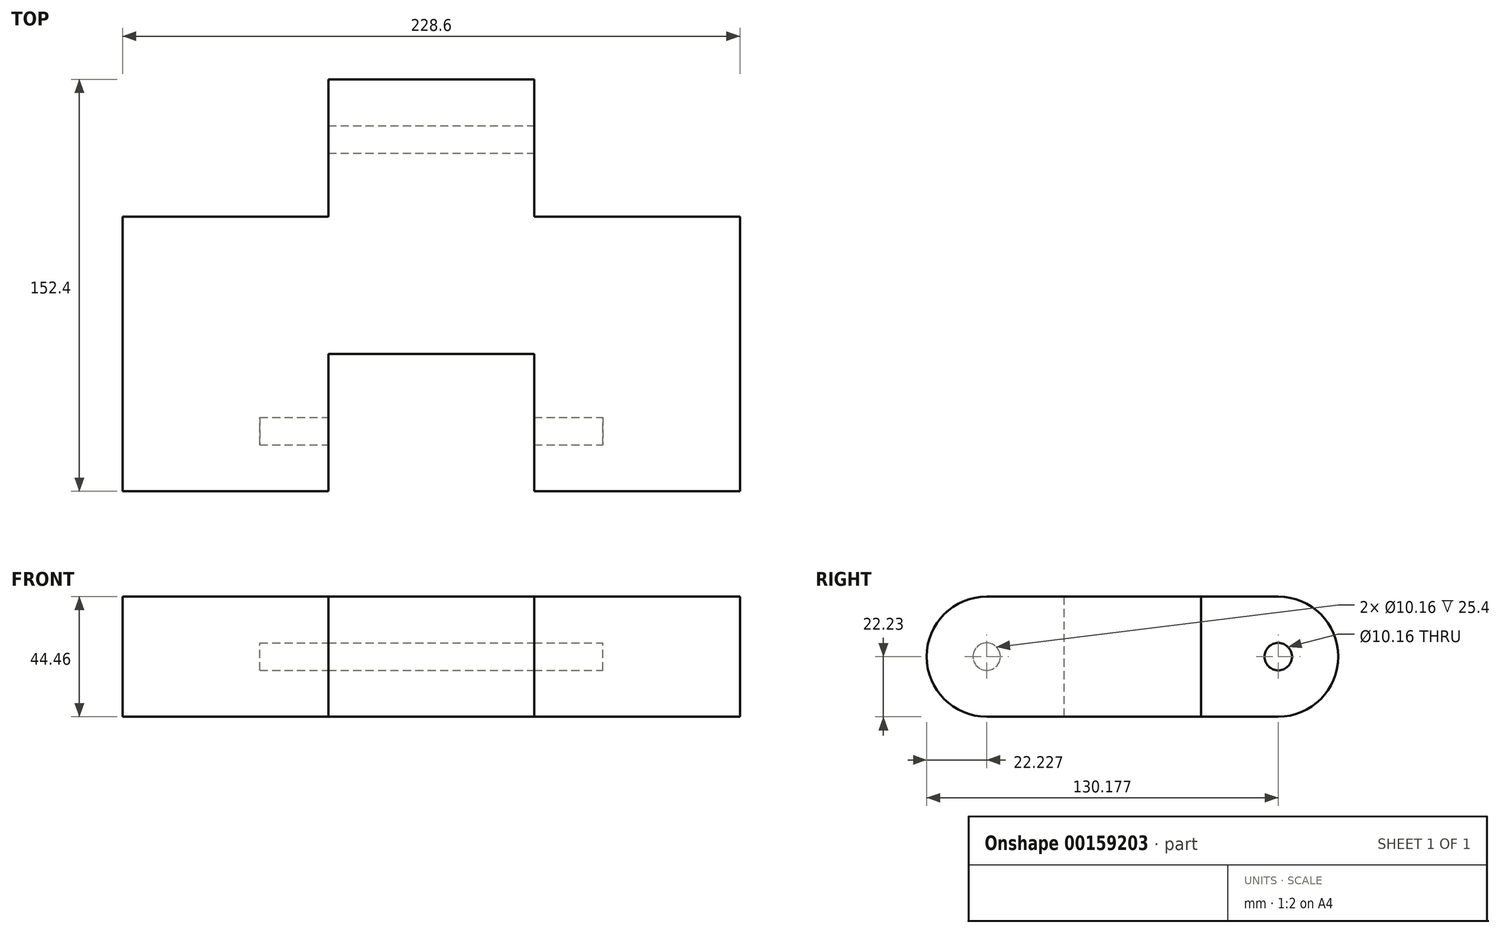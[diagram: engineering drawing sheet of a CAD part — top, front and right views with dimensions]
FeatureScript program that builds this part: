
annotation { "Feature Type Name" : "Feature", "Feature Type Description" : "" }
export const myFeature = defineFeature(function(context is Context, id is Id, definition is map)
    precondition{}
    {
        {
            var Q0;
            Q0=qCreatedBy(makeId("Top.planeOp"),FACE);
            var sketch = newSketch(context, id + "F0", { "sketchPlane" : qUnion([Q0])});
            skLineSegment(sketch, "E0", {"start": v(0, 40.67) * mm, "end": v(-38.1, 40.67) * mm});
            skLineSegment(sketch, "E1", {"start": v(-38.1, 40.67) * mm, "end": v(-38.1, -10.13) * mm});
            skLineSegment(sketch, "E2", {"start": v(-38.1, -10.13) * mm, "end": v(-114.3, -10.13) * mm});
            skLineSegment(sketch, "E3", {"start": v(-114.3, -10.13) * mm, "end": v(-114.3, -111.73) * mm});
            skLineSegment(sketch, "E4", {"start": v(-114.3, -111.73) * mm, "end": v(-38.1, -111.73) * mm});
            skLineSegment(sketch, "E5", {"start": v(-38.1, -111.73) * mm, "end": v(-38.1, -60.93) * mm});
            skLineSegment(sketch, "E6", {"start": v(-38.1, -60.93) * mm, "end": v(38.1, -60.93) * mm});
            skLineSegment(sketch, "E7", {"start": v(38.1, -60.93) * mm, "end": v(38.1, -111.73) * mm});
            skLineSegment(sketch, "E8", {"start": v(38.1, -111.73) * mm, "end": v(114.3, -111.73) * mm});
            skLineSegment(sketch, "E9", {"start": v(114.3, -111.73) * mm, "end": v(114.3, -10.13) * mm});
            skLineSegment(sketch, "E10", {"start": v(114.3, -10.13) * mm, "end": v(38.1, -10.13) * mm});
            skLineSegment(sketch, "E11", {"start": v(38.1, -10.13) * mm, "end": v(38.1, 40.67) * mm});
            skLineSegment(sketch, "E12", {"start": v(38.1, 40.67) * mm, "end": v(0, 40.67) * mm});
            skSolve(sketch);
        }
        {
            var Q0;
            Q0=makeQuery(id+"F0.imprint","IMPRINT",FACE,{"disambiguationData":[TD([[makeQuery(id+"F0.imprint","IMPRINT",EDGE,{"derivedFrom":sQuery(id+"F0.wireOp",EDGE,"E0")}),1.0]])]});
            extrude(context, id + "F1", {"entities" : qUnion([Q0]), "endBound" : BoundingType.SYMMETRIC, "depth" : 44.45 * mm});
        }
        {
            var Q0;
            Q0=makeQuery(id+"F1.opExtrude","CAP_EDGE",EDGE,{"disambiguationData":[OSD([sQuery(id+"F0.wireOp",EDGE,"E4")])],"isStart":false});
            var Q1;
            Q1=makeQuery(id+"F1.opExtrude","CAP_EDGE",EDGE,{"disambiguationData":[OSD([sQuery(id+"F0.wireOp",EDGE,"E4")])],"isStart":true});
            var Q2;
            Q2=makeQuery(id+"F1.opExtrude","CAP_EDGE",EDGE,{"disambiguationData":[OSD([sQuery(id+"F0.wireOp",EDGE,"E8")])],"isStart":false});
            var Q3;
            Q3=makeQuery(id+"F1.opExtrude","CAP_EDGE",EDGE,{"disambiguationData":[OSD([sQuery(id+"F0.wireOp",EDGE,"E8")])],"isStart":true});
            var Q4;
            Q4=makeQuery(id+"F1.opExtrude","CAP_EDGE",EDGE,{"disambiguationData":[OSD([sQuery(id+"F0.wireOp",EDGE,"E0"),sQuery(id+"F0.wireOp",EDGE,"E12")])],"isStart":false});
            var Q5;
            Q5=makeQuery(id+"F1.opExtrude","CAP_EDGE",EDGE,{"disambiguationData":[OSD([sQuery(id+"F0.wireOp",EDGE,"E0"),sQuery(id+"F0.wireOp",EDGE,"E12")])],"isStart":true});
            fillet(context, id + "F2", {"entities" : qUnion([Q0, Q1, Q2, Q3, Q4, Q5]), "radius" : 22.22 * mm, "tangentPropagation" : true, "allowEdgeOverflow" : false});
        }
        {
            var Q0;
            Q0=qCreatedBy(makeId("Right.planeOp"),FACE);
            var sketch = newSketch(context, id + "F3", { "sketchPlane" : qUnion([Q0])});
            skCircle(sketch, "E13", {"center": v(18.45, 0) * mm, "radius": 5.08 * mm});
            skSolve(sketch);
        }
        {
            var Q0;
            Q0 = qSketchRegion(id + "F3", true);
            extrude(context, id + "F4", {"entities" : qUnion([Q0]), "operationType" : NewBodyOperationType.REMOVE, "endBound" : BoundingType.THROUGH_ALL, "oppositeDirection" : true, "depth" : 25.4 * mm});
        }
        {
            var Q0;
            Q0 = qSketchRegion(id + "F3", true);
            extrude(context, id + "F5", {"entities" : qUnion([Q0]), "operationType" : NewBodyOperationType.REMOVE, "endBound" : BoundingType.THROUGH_ALL, "depth" : 25.4 * mm});
        }
        {
            var Q0;
            Q0=qCreatedBy(makeId("Right.planeOp"),FACE);
            var sketch = newSketch(context, id + "F6", { "sketchPlane" : qUnion([Q0])});
            skCircle(sketch, "E14", {"center": v(-89.5, 0) * mm, "radius": 5.08 * mm});
            skSolve(sketch);
        }
        {
            var Q0;
            Q0 = qSketchRegion(id + "F6", true);
            extrude(context, id + "F7", {"entities" : qUnion([Q0]), "operationType" : NewBodyOperationType.REMOVE, "endBound" : BoundingType.SYMMETRIC, "oppositeDirection" : true, "depth" : 127 * mm});
        }
    });
